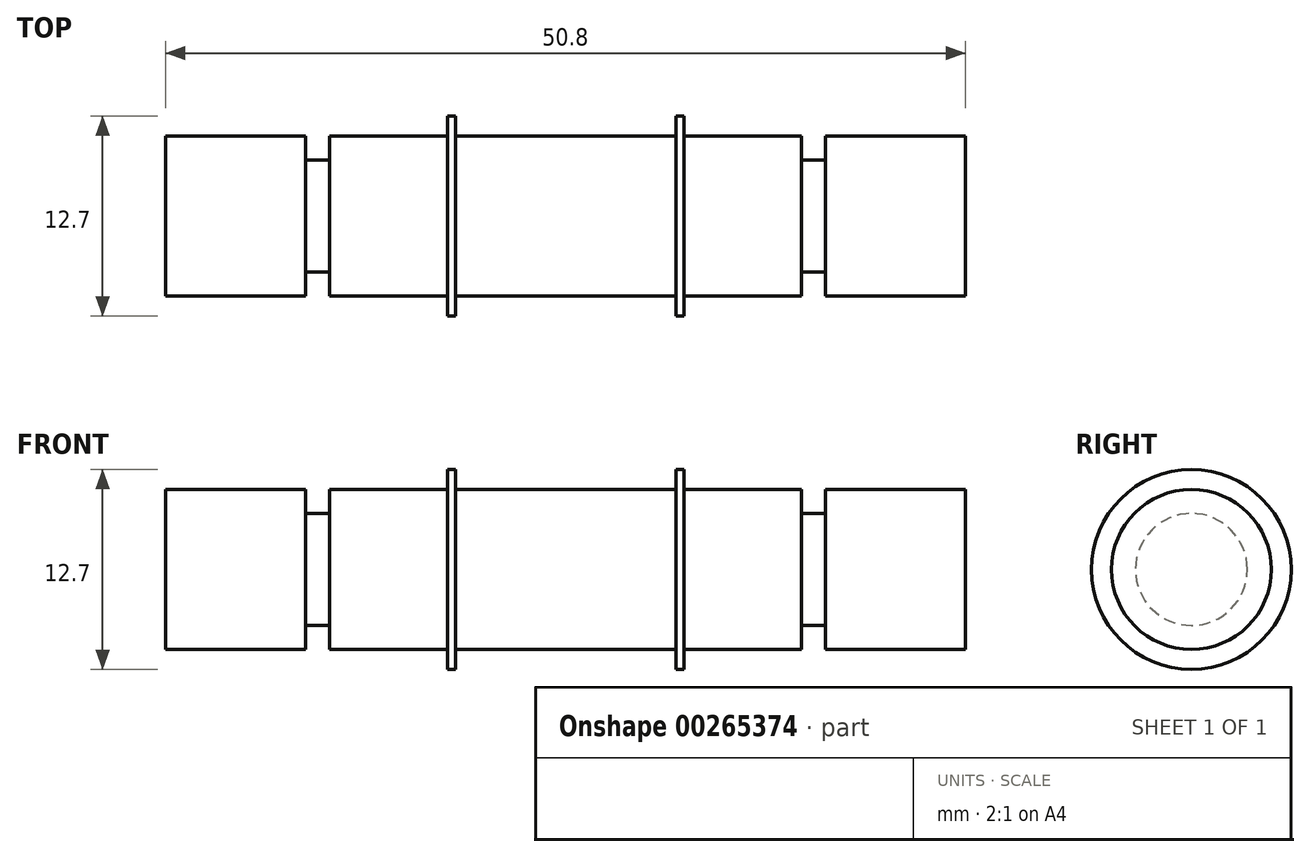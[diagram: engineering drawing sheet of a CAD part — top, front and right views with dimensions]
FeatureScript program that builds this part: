
annotation { "Feature Type Name" : "Feature", "Feature Type Description" : "" }
export const myFeature = defineFeature(function(context is Context, id is Id, definition is map)
    precondition{}
    {
        {
            var Q0;
            Q0=qCreatedBy(makeId("Front.planeOp"),FACE);
            var sketch = newSketch(context, id + "F0", { "sketchPlane" : qUnion([Q0])});
            skLineSegment(sketch, "E0", {"start": v(0, 0) * mm, "end": v(0, 5.08) * mm});
            skLineSegment(sketch, "E1", {"start": v(0, 5.08) * mm, "end": v(8.9, 5.08) * mm});
            skLineSegment(sketch, "E2", {"start": v(8.89, 5.08) * mm, "end": v(8.89, 3.56) * mm});
            skLineSegment(sketch, "E3", {"start": v(8.9, 3.56) * mm, "end": v(10.41, 3.56) * mm});
            skLineSegment(sketch, "E4", {"start": v(10.41, 3.56) * mm, "end": v(10.41, 5.08) * mm});
            skLineSegment(sketch, "E5", {"start": v(10.41, 5.08) * mm, "end": v(40.39, 5.08) * mm});
            skLineSegment(sketch, "E6", {"start": v(40.39, 5.08) * mm, "end": v(40.39, 3.56) * mm});
            skLineSegment(sketch, "E7", {"start": v(40.39, 3.56) * mm, "end": v(41.91, 3.56) * mm});
            skLineSegment(sketch, "E8", {"start": v(41.91, 3.56) * mm, "end": v(41.91, 5.08) * mm});
            skLineSegment(sketch, "E9", {"start": v(41.91, 5.08) * mm, "end": v(50.8, 5.08) * mm});
            skLineSegment(sketch, "E10", {"start": v(50.8, 5.08) * mm, "end": v(50.8, 0) * mm});
            skLineSegment(sketch, "E11", {"start": v(50.8, 0) * mm, "end": v(0, 0) * mm});
            skSolve(sketch);
        }
        {
            var Q0;
            Q0 = qSketchRegion(id + "F0", true);
            var Q1;
            Q1=sQuery(id+"F0.wireOp",EDGE,"E11");
            revolve(context, id + "F1", {"entities" : qUnion([Q0]), "axis" : qUnion([Q1]), "revolveType" : RevolveType.FULL});
        }
        {
            var Q0;
            Q0=qCreatedBy(makeId("Right.planeOp"),FACE);
            cPlane(context, id + "F2", {"entities" : qUnion([Q0]), "cplaneType" : CPlaneType.OFFSET, "offset" : 25.4 * mm, "width" : 152.4 * mm, "height" : 152.4 * mm});
        }
        {
            var Q0;
            Q0=qCreatedBy(id+"F2.planeOp",FACE);
            cPlane(context, id + "F3", {"entities" : qUnion([Q0]), "cplaneType" : CPlaneType.OFFSET, "offset" : 7 * mm, "width" : 150 * mm, "height" : 150 * mm});
        }
        {
            var Q0;
            Q0=qCreatedBy(id+"F2.planeOp",FACE);
            cPlane(context, id + "F4", {"entities" : qUnion([Q0]), "cplaneType" : CPlaneType.OFFSET, "offset" : 7 * mm, "oppositeDirection" : true, "width" : 150 * mm, "height" : 150 * mm});
        }
        {
            var Q0;
            Q0=qCreatedBy(id+"F3.planeOp",FACE);
            var sketch = newSketch(context, id + "F5", { "sketchPlane" : qUnion([Q0])});
            skCircle(sketch, "E12", {"center": v(0, 0) * mm, "radius": 6.35 * mm});
            skSolve(sketch);
        }
        {
            var Q0;
            Q0 = qSketchRegion(id + "F5", true);
            extrude(context, id + "F6", {"entities" : qUnion([Q0]), "operationType" : NewBodyOperationType.ADD, "depth" : 0.5 * mm});
        }
        {
            var Q0;
            Q0=qCreatedBy(id+"F4.planeOp",FACE);
            var sketch = newSketch(context, id + "F7", { "sketchPlane" : qUnion([Q0])});
            skCircle(sketch, "E13.0", {"center": v(0, 0) * mm, "radius": 6.35 * mm});
            skSolve(sketch);
        }
        {
            var Q0;
            Q0 = qSketchRegion(id + "F7", true);
            extrude(context, id + "F8", {"entities" : qUnion([Q0]), "operationType" : NewBodyOperationType.ADD, "oppositeDirection" : true, "depth" : 0.5 * mm});
        }
    });
